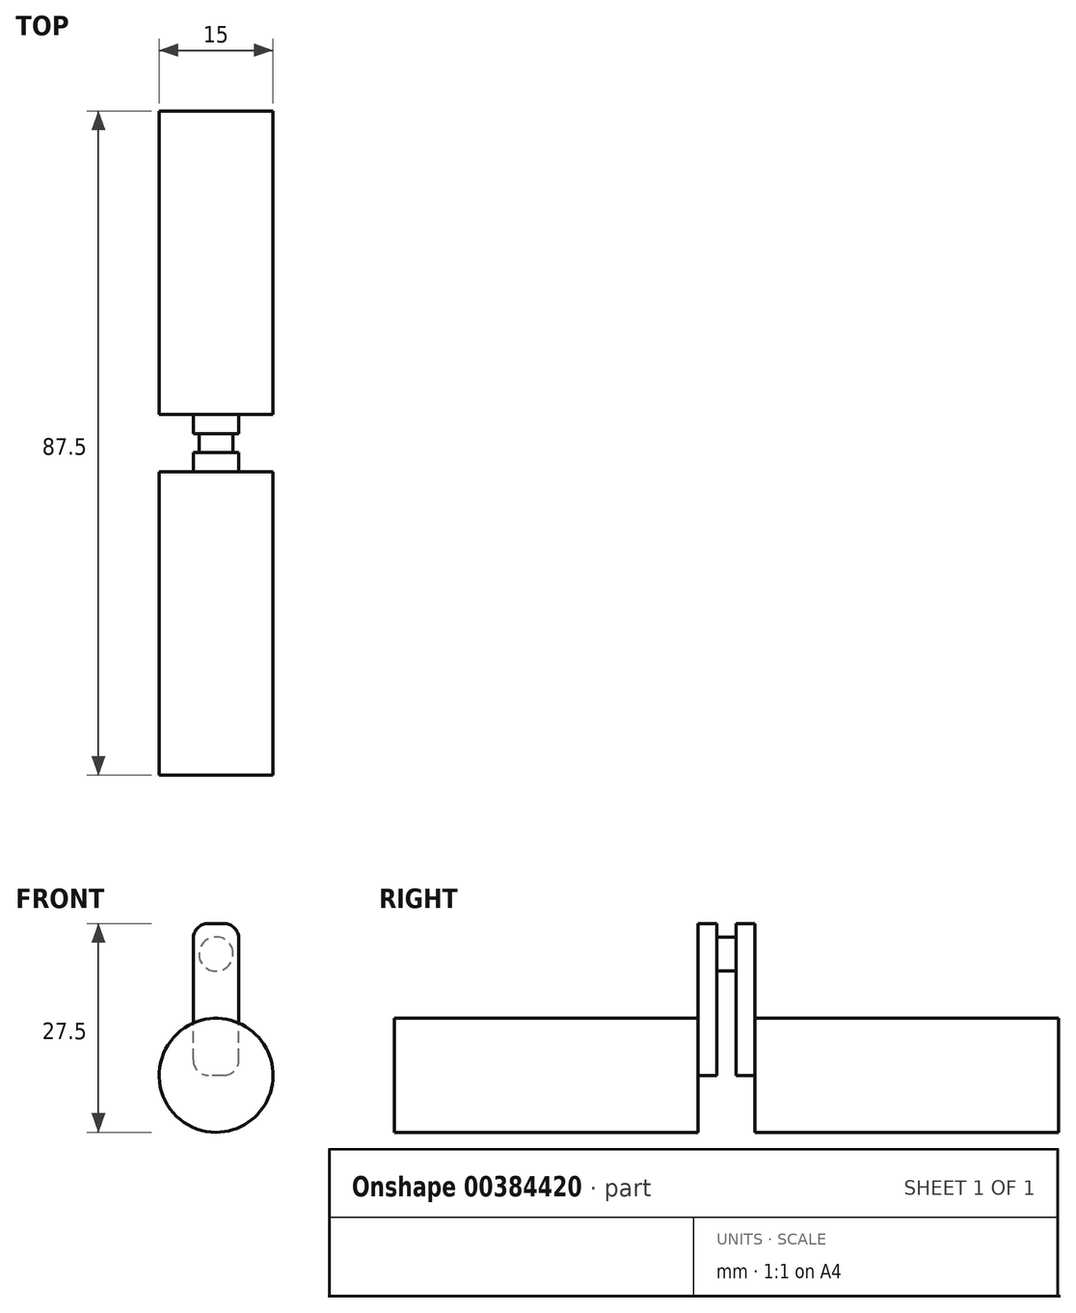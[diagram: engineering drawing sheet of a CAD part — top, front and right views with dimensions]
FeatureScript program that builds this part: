
annotation { "Feature Type Name" : "Feature", "Feature Type Description" : "" }
export const myFeature = defineFeature(function(context is Context, id is Id, definition is map)
    precondition{}
    {
        {
            var Q0;
            Q0=qCreatedBy(makeId("Front.planeOp"),FACE);
            var sketch = newSketch(context, id + "F0", { "sketchPlane" : qUnion([Q0])});
            skCircle(sketch, "E0", {"center": v(0, 0) * mm, "radius": 7.5 * mm});
            skSolve(sketch);
        }
        {
            var Q0;
            Q0=makeQuery(id+"F0.imprint","IMPRINT",FACE,{"disambiguationData":[TD([[makeQuery(id+"F0.imprint","IMPRINT",EDGE,{"derivedFrom":sQuery(id+"F0.wireOp",EDGE,"E0")}),1.0]])]});
            extrude(context, id + "F1", {"entities" : qUnion([Q0]), "depth" : 40 * mm});
        }
        {
            var Q0;
            Q0=makeQuery(id+"F1.opExtrude","CAP_FACE",FACE,{"disambiguationData":[OSD([sQuery(id+"F0.wireOp",EDGE,"E0")])],"isStart":true});
            var sketch = newSketch(context, id + "F2", { "sketchPlane" : qUnion([Q0])});
            skLineSegment(sketch, "E1.top", {"start": v(-3, 20) * mm, "end": v(3, 20) * mm});
            skLineSegment(sketch, "E1.left", {"start": v(-3, 0) * mm, "end": v(-3, 20) * mm});
            skLineSegment(sketch, "E1.right", {"start": v(3, 0) * mm, "end": v(3, 20) * mm});
            skLineSegment(sketch, "E2", {"start": v(-3, 0) * mm, "end": v(3, 0) * mm});
            skSolve(sketch);
        }
        {
            var Q0;
            {var subQ0=sQuery(id+"F2.wireOp",EDGE,"E1.top");Q0=makeQuery(id+"F2.imprint","IMPRINT",FACE,{"disambiguationData":[TD([[makeQuery(id+"F2.imprint","IMPRINT",EDGE,{"derivedFrom":subQ0}),-1.0]])]});}
            var Q1;
            {var subQ0=sQuery(id+"F2.wireOp",EDGE,"E2");Q1=makeQuery(id+"F2.imprint","IMPRINT",FACE,{"disambiguationData":[TD([[makeQuery(id+"F2.imprint","IMPRINT",EDGE,{"derivedFrom":subQ0}),1.0]])]});}
            extrude(context, id + "F3", {"entities" : qUnion([Q0, Q1]), "operationType" : NewBodyOperationType.ADD, "depth" : 2.5 * mm});
        }
        {
            var Q0;
            Q0=makeQuery(id+"F3.opExtrude","SWEPT_EDGE",EDGE,{"disambiguationData":[OSD([sQuery(id+"F2.wireOp",EDGE,"E1.top"),sQuery(id+"F2.wireOp",EDGE,"E1.left")])]});
            var Q1;
            Q1=makeQuery(id+"F3.opExtrude","SWEPT_EDGE",EDGE,{"disambiguationData":[OSD([sQuery(id+"F2.wireOp",EDGE,"E1.top"),sQuery(id+"F2.wireOp",EDGE,"E1.right")])]});
            var Q2;
            Q2=makeQuery(id+"F3.opExtrude","SWEPT_EDGE",EDGE,{"disambiguationData":[OSD([sQuery(id+"F2.wireOp",EDGE,"E1.left"),sQuery(id+"F2.wireOp",EDGE,"E2")])]});
            var Q3;
            Q3=makeQuery(id+"F3.opExtrude","SWEPT_EDGE",EDGE,{"disambiguationData":[OSD([sQuery(id+"F2.wireOp",EDGE,"E1.right"),sQuery(id+"F2.wireOp",EDGE,"E2")])]});
            fillet(context, id + "F4", {"entities" : qUnion([Q0, Q1, Q2, Q3]), "radius" : 2 * mm, "tangentPropagation" : true, "allowEdgeOverflow" : false});
        }
        {
            var Q0;
            Q0=makeQuery(id+"F3.opExtrude","CAP_FACE",FACE,{"disambiguationData":[OSD([sQuery(id+"F2.wireOp",EDGE,"E1.top"),sQuery(id+"F2.wireOp",EDGE,"E1.left"),sQuery(id+"F2.wireOp",EDGE,"E1.right"),sQuery(id+"F2.wireOp",EDGE,"E2")])],"isStart":false});
            var sketch = newSketch(context, id + "F5", { "sketchPlane" : qUnion([Q0])});
            skCircle(sketch, "E3", {"center": v(0, 15.97) * mm, "radius": 2.25 * mm});
            skSolve(sketch);
        }
        {
            var Q0;
            Q0=makeQuery(id+"F5.imprint","IMPRINT",FACE,{"disambiguationData":[TD([[makeQuery(id+"F5.imprint","IMPRINT",EDGE,{"derivedFrom":sQuery(id+"F5.wireOp",EDGE,"E3")}),1.0]])]});
            extrude(context, id + "F6", {"entities" : qUnion([Q0]), "operationType" : NewBodyOperationType.ADD, "depth" : 2.5 * mm});
        }
        {
            var Q0;
            Q0=makeQuery(id+"F6.opExtrude","CAP_FACE",FACE,{"disambiguationData":[OSD([sQuery(id+"F5.wireOp",EDGE,"E3")])],"isStart":false});
            var sketch = newSketch(context, id + "F7", { "sketchPlane" : qUnion([Q0])});
            skLineSegment(sketch, "E4.bottom", {"start": v(3, 0) * mm, "end": v(-3, 0) * mm});
            skLineSegment(sketch, "E4.top", {"start": v(3, 20) * mm, "end": v(-3, 20) * mm});
            skLineSegment(sketch, "E4.left", {"start": v(3, 0) * mm, "end": v(3, 20) * mm});
            skLineSegment(sketch, "E4.right", {"start": v(-3, 0) * mm, "end": v(-3, 20) * mm});
            skPoint(sketch, "E4.middle", {"position": v(0, 10) * mm});
            skSolve(sketch);
        }
        {
            var Q0;
            Q0=makeQuery(id+"F7.imprint","IMPRINT",FACE,{"disambiguationData":[TD([[makeQuery(id+"F7.imprint","IMPRINT",EDGE,{"derivedFrom":sQuery(id+"F7.wireOp",EDGE,"E4.bottom")}),-1.0]])]});
            var Q1;
            Q1=makeQuery(id+"F7.imprint","IMPRINT",FACE,{"disambiguationData":[TD([[makeQuery(id+"F7.imprint","IMPRINT",EDGE,{"derivedFrom":makeQuery(id+"F6.opExtrude","CAP_EDGE",EDGE,{"disambiguationData":[OSD([sQuery(id+"F5.wireOp",EDGE,"E3")])],"isStart":false})}),1.0]])]});
            extrude(context, id + "F8", {"entities" : qUnion([Q0, Q1]), "operationType" : NewBodyOperationType.ADD, "depth" : 2.5 * mm});
        }
        {
            var Q0;
            Q0=makeQuery(id+"F8.opExtrude","SWEPT_EDGE",EDGE,{"disambiguationData":[OSD([sQuery(id+"F7.wireOp",EDGE,"E4.top"),sQuery(id+"F7.wireOp",EDGE,"E4.right")])]});
            var Q1;
            Q1=makeQuery(id+"F8.opExtrude","SWEPT_EDGE",EDGE,{"disambiguationData":[OSD([sQuery(id+"F7.wireOp",EDGE,"E4.top"),sQuery(id+"F7.wireOp",EDGE,"E4.left")])]});
            var Q2;
            Q2=makeQuery(id+"F8.opExtrude","SWEPT_EDGE",EDGE,{"disambiguationData":[OSD([sQuery(id+"F7.wireOp",EDGE,"E4.bottom"),sQuery(id+"F7.wireOp",EDGE,"E4.right")])]});
            var Q3;
            Q3=makeQuery(id+"F8.opExtrude","SWEPT_EDGE",EDGE,{"disambiguationData":[OSD([sQuery(id+"F7.wireOp",EDGE,"E4.bottom"),sQuery(id+"F7.wireOp",EDGE,"E4.left")])]});
            fillet(context, id + "F9", {"entities" : qUnion([Q0, Q1, Q2, Q3]), "radius" : 2 * mm, "tangentPropagation" : true, "allowEdgeOverflow" : false});
        }
        {
            var Q0;
            Q0=makeQuery(id+"F8.opExtrude","CAP_FACE",FACE,{"disambiguationData":[OSD([sQuery(id+"F7.wireOp",EDGE,"E4.bottom"),sQuery(id+"F7.wireOp",EDGE,"E4.top"),sQuery(id+"F7.wireOp",EDGE,"E4.left"),sQuery(id+"F7.wireOp",EDGE,"E4.right")])],"isStart":false});
            var sketch = newSketch(context, id + "F10", { "sketchPlane" : qUnion([Q0])});
            skCircle(sketch, "E5", {"center": v(0, 0) * mm, "radius": 7.5 * mm});
            skSolve(sketch);
        }
        {
            var Q0;
            {var subQ2=sQuery(id+"F7.wireOp",EDGE,"E4.bottom");Q0=makeQuery(id+"F10.imprint","IMPRINT",FACE,{"disambiguationData":[TD([[makeQuery(id+"F10.imprint","IMPRINT",EDGE,{"derivedFrom":makeQuery(id+"F8.opExtrude","CAP_EDGE",EDGE,{"disambiguationData":[OSD([subQ2])],"isStart":false})}),1.0]])]});}
            var Q1;
            {var subQ0=sQuery(id+"F7.wireOp",EDGE,"E4.bottom");Q1=makeQuery(id+"F10.imprint","IMPRINT",FACE,{"disambiguationData":[TD([[makeQuery(id+"F10.imprint","IMPRINT",EDGE,{"derivedFrom":makeQuery(id+"F8.opExtrude","CAP_EDGE",EDGE,{"disambiguationData":[OSD([subQ0])],"isStart":false})}),-1.0]])]});}
            extrude(context, id + "F11", {"entities" : qUnion([Q0, Q1]), "operationType" : NewBodyOperationType.ADD, "depth" : 40 * mm});
        }
    });
